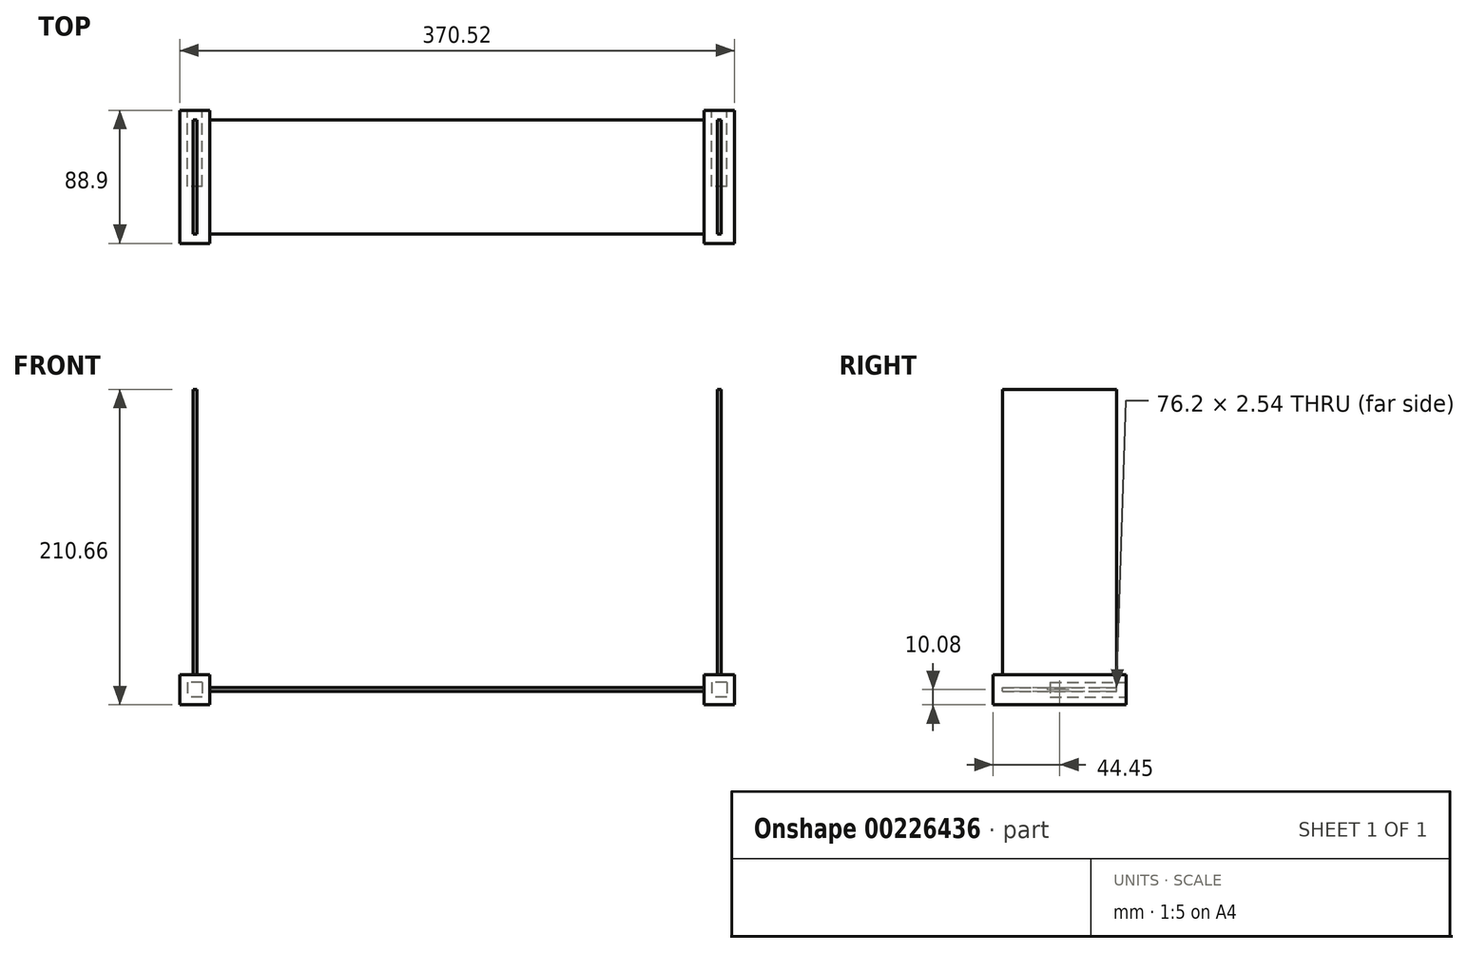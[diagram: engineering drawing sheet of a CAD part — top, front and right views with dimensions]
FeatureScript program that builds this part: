
annotation { "Feature Type Name" : "Feature", "Feature Type Description" : "" }
export const myFeature = defineFeature(function(context is Context, id is Id, definition is map)
    precondition{}
    {
        {
            var Q0;
            Q0=qCreatedBy(makeId("Front.planeOp"),FACE);
            var sketch = newSketch(context, id + "F0", { "sketchPlane" : qUnion([Q0])});
            skLineSegment(sketch, "E0.bottom", {"start": v(-199.36, 5) * mm, "end": v(-209.36, 5) * mm});
            skLineSegment(sketch, "E0.top", {"start": v(-199.36, -5) * mm, "end": v(-209.36, -5) * mm});
            skLineSegment(sketch, "E0.left", {"start": v(-199.36, 5) * mm, "end": v(-199.36, -5) * mm});
            skLineSegment(sketch, "E0.right", {"start": v(-209.36, 5) * mm, "end": v(-209.36, -5) * mm});
            skPoint(sketch, "E0.middle", {"position": v(-204.36, 0) * mm});
            skLineSegment(sketch, "E1.bottom", {"start": v(151, 5) * mm, "end": v(141, 5) * mm});
            skLineSegment(sketch, "E1.top", {"start": v(151, -5) * mm, "end": v(141, -5) * mm});
            skLineSegment(sketch, "E1.left", {"start": v(151, 5) * mm, "end": v(151, -5) * mm});
            skLineSegment(sketch, "E1.right", {"start": v(141, 5) * mm, "end": v(141, -5) * mm});
            skPoint(sketch, "E1.middle", {"position": v(146, 0) * mm});
            skLineSegment(sketch, "E2.0", {"start": v(-194.28, 10.08) * mm, "end": v(-194.28, -10.08) * mm});
            skLineSegment(sketch, "E2.1", {"start": v(-194.28, 10.08) * mm, "end": v(-214.44, 10.08) * mm});
            skLineSegment(sketch, "E2.2", {"start": v(-214.44, 10.08) * mm, "end": v(-214.44, -10.08) * mm});
            skLineSegment(sketch, "E2.3", {"start": v(-194.28, -10.08) * mm, "end": v(-214.44, -10.08) * mm});
            skLineSegment(sketch, "E3.0", {"start": v(156.08, 10.08) * mm, "end": v(135.92, 10.08) * mm});
            skLineSegment(sketch, "E3.1", {"start": v(156.08, 10.08) * mm, "end": v(156.08, -10.08) * mm});
            skLineSegment(sketch, "E3.2", {"start": v(156.08, -10.08) * mm, "end": v(135.92, -10.08) * mm});
            skLineSegment(sketch, "E3.3", {"start": v(135.92, 10.08) * mm, "end": v(135.92, -10.08) * mm});
            skLineSegment(sketch, "E4", {"start": v(146, 10.08) * mm, "end": v(146, 5) * mm, "construction": true});
            skLineSegment(sketch, "E5", {"start": v(-199.36, 1.43) * mm, "end": v(-194.28, 1.43) * mm, "construction": true});
            skSolve(sketch);
        }
        {
            var Q0;
            Q0=makeQuery(id+"F0.imprint","IMPRINT",FACE,{"disambiguationData":[TD([[makeQuery(id+"F0.imprint","IMPRINT",EDGE,{"derivedFrom":sQuery(id+"F0.wireOp",EDGE,"E0.bottom")}),1.0]])]});
            var Q1;
            Q1=makeQuery(id+"F0.imprint","IMPRINT",FACE,{"disambiguationData":[TD([[makeQuery(id+"F0.imprint","IMPRINT",EDGE,{"derivedFrom":sQuery(id+"F0.wireOp",EDGE,"E0.bottom")}),-1.0]])]});
            var Q2;
            Q2=makeQuery(id+"F0.imprint","IMPRINT",FACE,{"disambiguationData":[TD([[makeQuery(id+"F0.imprint","IMPRINT",EDGE,{"derivedFrom":sQuery(id+"F0.wireOp",EDGE,"E1.bottom")}),1.0]])]});
            var Q3;
            Q3=makeQuery(id+"F0.imprint","IMPRINT",FACE,{"disambiguationData":[TD([[makeQuery(id+"F0.imprint","IMPRINT",EDGE,{"derivedFrom":sQuery(id+"F0.wireOp",EDGE,"E1.bottom")}),-1.0]])]});
            extrude(context, id + "F1", {"entities" : qUnion([Q0, Q1, Q2, Q3]), "depth" : 88.9 * mm, "offsetDistance" : 25.4 * mm});
        }
        {
            var Q0;
            Q0=makeQuery(id+"F0.imprint","IMPRINT",FACE,{"disambiguationData":[TD([[makeQuery(id+"F0.imprint","IMPRINT",EDGE,{"derivedFrom":sQuery(id+"F0.wireOp",EDGE,"E0.bottom")}),1.0]])]});
            var Q1;
            Q1=makeQuery(id+"F0.imprint","IMPRINT",FACE,{"disambiguationData":[TD([[makeQuery(id+"F0.imprint","IMPRINT",EDGE,{"derivedFrom":sQuery(id+"F0.wireOp",EDGE,"E1.bottom")}),1.0]])]});
            extrude(context, id + "F2", {"entities" : qUnion([Q0, Q1]), "operationType" : NewBodyOperationType.REMOVE, "depth" : 50.8 * mm, "offsetDistance" : 25.4 * mm});
        }
        {
            var Q0;
            Q0=makeQuery(id+"F1.opExtrude","SWEPT_FACE",FACE,{"disambiguationData":[OSD([sQuery(id+"F0.wireOp",EDGE,"E3.3")])]});
            var sketch = newSketch(context, id + "F3", { "sketchPlane" : qUnion([Q0])});
            skLineSegment(sketch, "E6.bottom", {"start": v(6.35, 1.27) * mm, "end": v(82.55, 1.27) * mm});
            skLineSegment(sketch, "E6.top", {"start": v(6.35, -1.27) * mm, "end": v(82.55, -1.27) * mm});
            skLineSegment(sketch, "E6.left", {"start": v(6.35, 1.27) * mm, "end": v(6.35, -1.27) * mm});
            skLineSegment(sketch, "E6.right", {"start": v(82.55, 1.27) * mm, "end": v(82.55, -1.27) * mm});
            skPoint(sketch, "E7", {"position": v(44.45, 1.27) * mm});
            skPoint(sketch, "E8", {"position": v(82.55, 0) * mm});
            skSolve(sketch);
        }
        {
            var Q0;
            Q0=makeQuery(id+"F3.imprint","IMPRINT",FACE,{"disambiguationData":[TD([[makeQuery(id+"F3.imprint","IMPRINT",EDGE,{"derivedFrom":sQuery(id+"F3.wireOp",EDGE,"E6.bottom")}),-1.0]])]});
            extrude(context, id + "F4", {"entities" : qUnion([Q0]), "operationType" : NewBodyOperationType.ADD, "endBound" : BoundingType.UP_TO_NEXT, "depth" : 25.4 * mm, "offsetDistance" : 25.4 * mm});
        }
        {
            var Q0;
            Q0=makeQuery(id+"F1.opExtrude","SWEPT_FACE",FACE,{"disambiguationData":[OSD([sQuery(id+"F0.wireOp",EDGE,"E3.0")])]});
            var sketch = newSketch(context, id + "F5", { "sketchPlane" : qUnion([Q0])});
            skLineSegment(sketch, "E9.bottom", {"start": v(-205.63, -6.35) * mm, "end": v(-203.1, -6.35) * mm});
            skLineSegment(sketch, "E9.top", {"start": v(-205.63, -82.55) * mm, "end": v(-203.1, -82.55) * mm});
            skLineSegment(sketch, "E9.left", {"start": v(-205.63, -6.35) * mm, "end": v(-205.63, -82.55) * mm});
            skLineSegment(sketch, "E9.right", {"start": v(-203.1, -6.35) * mm, "end": v(-203.1, -82.55) * mm});
            skLineSegment(sketch, "E10.bottom", {"start": v(144.73, -82.55) * mm, "end": v(147.27, -82.55) * mm});
            skLineSegment(sketch, "E10.top", {"start": v(144.73, -6.35) * mm, "end": v(147.27, -6.35) * mm});
            skLineSegment(sketch, "E10.left", {"start": v(144.73, -6.35) * mm, "end": v(144.73, -82.55) * mm});
            skLineSegment(sketch, "E10.right", {"start": v(147.27, -6.35) * mm, "end": v(147.27, -82.55) * mm});
            skPoint(sketch, "E11", {"position": v(-203.1, -44.45) * mm});
            skPoint(sketch, "E12", {"position": v(-204.36, -6.35) * mm});
            skPoint(sketch, "E13", {"position": v(146, -82.55) * mm});
            skPoint(sketch, "E14", {"position": v(144.73, -44.45) * mm});
            skSolve(sketch);
        }
        {
            var Q0;
            Q0 = qSketchRegion(id + "F5", true);
            extrude(context, id + "F6", {"entities" : qUnion([Q0]), "operationType" : NewBodyOperationType.ADD, "depth" : 190.5 * mm, "offsetDistance" : 25.4 * mm});
        }
    });
